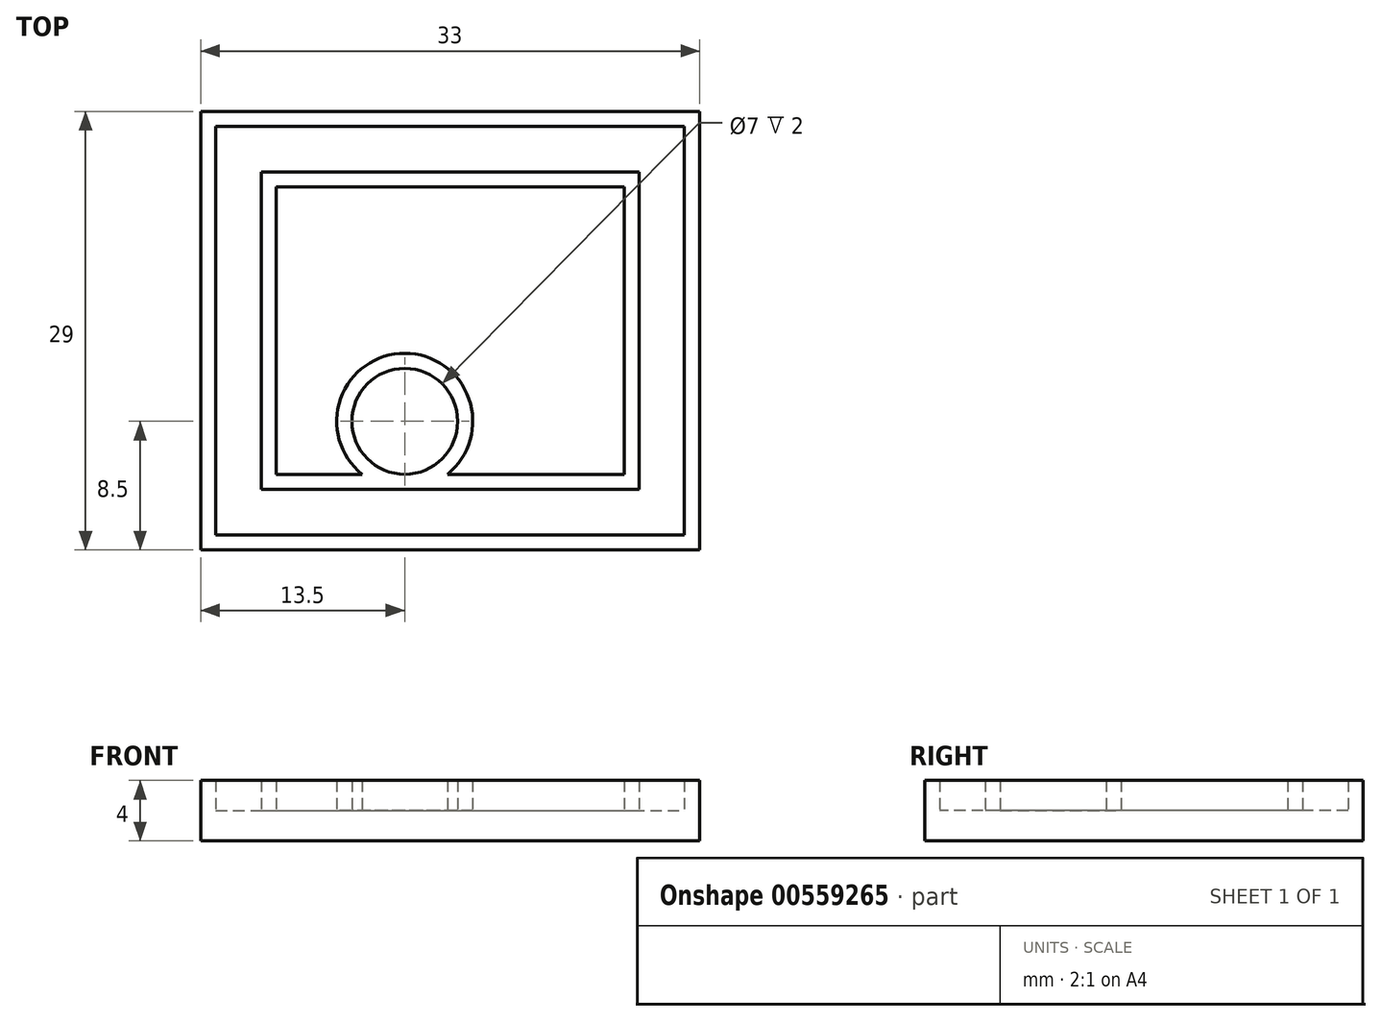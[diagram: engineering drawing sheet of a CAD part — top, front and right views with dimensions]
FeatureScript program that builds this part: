
annotation { "Feature Type Name" : "Feature", "Feature Type Description" : "" }
export const myFeature = defineFeature(function(context is Context, id is Id, definition is map)
    precondition{}
    {
        {
            var Q0;
            Q0=qCreatedBy(makeId("Top.planeOp"),FACE);
            var sketch = newSketch(context, id + "F0", { "sketchPlane" : qUnion([Q0])});
            skLineSegment(sketch, "E0.bottom", {"start": v(-16.5, 14.5) * mm, "end": v(16.5, 14.5) * mm});
            skLineSegment(sketch, "E0.top", {"start": v(-16.5, -14.5) * mm, "end": v(16.5, -14.5) * mm});
            skLineSegment(sketch, "E0.left", {"start": v(-16.5, 14.5) * mm, "end": v(-16.5, -14.5) * mm});
            skLineSegment(sketch, "E0.right", {"start": v(16.5, 14.5) * mm, "end": v(16.5, -14.5) * mm});
            skPoint(sketch, "E0.middle", {"position": v(0, 0) * mm});
            skSolve(sketch);
        }
        {
            var Q0;
            Q0 = qSketchRegion(id + "F0", true);
            extrude(context, id + "F1", {"entities" : qUnion([Q0]), "depth" : 2 * mm, "offsetDistance" : 25 * mm});
        }
        {
            var Q0;
            Q0=makeQuery(id+"F1.opExtrude","CAP_FACE",FACE,{"disambiguationData":[OSD([sQuery(id+"F0.wireOp",EDGE,"E0.bottom"),sQuery(id+"F0.wireOp",EDGE,"E0.top"),sQuery(id+"F0.wireOp",EDGE,"E0.left"),sQuery(id+"F0.wireOp",EDGE,"E0.right")])],"isStart":false});
            var sketch = newSketch(context, id + "F2", { "sketchPlane" : qUnion([Q0])});
            skLineSegment(sketch, "E1.bottom", {"start": v(-16.5, 14.5) * mm, "end": v(16.5, 14.5) * mm});
            skLineSegment(sketch, "E1.top", {"start": v(-16.5, -14.5) * mm, "end": v(16.5, -14.5) * mm});
            skLineSegment(sketch, "E1.left", {"start": v(-16.5, 14.5) * mm, "end": v(-16.5, -14.5) * mm});
            skLineSegment(sketch, "E1.right", {"start": v(16.5, 14.5) * mm, "end": v(16.5, -14.5) * mm});
            skLineSegment(sketch, "E2.bottom", {"start": v(-15.5, 13.5) * mm, "end": v(15.5, 13.5) * mm});
            skLineSegment(sketch, "E2.top", {"start": v(-15.5, -13.5) * mm, "end": v(15.5, -13.5) * mm});
            skLineSegment(sketch, "E2.left", {"start": v(-15.5, 13.5) * mm, "end": v(-15.5, -13.5) * mm});
            skLineSegment(sketch, "E2.right", {"start": v(15.5, 13.5) * mm, "end": v(15.5, -13.5) * mm});
            skLineSegment(sketch, "E3", {"start": v(-15.5, 13.5) * mm, "end": v(15.5, -13.5) * mm, "construction": true});
            skSolve(sketch);
        }
        {
            var Q0;
            Q0 = qSketchRegion(id + "F2", true);
            extrude(context, id + "F3", {"entities" : qUnion([Q0]), "operationType" : NewBodyOperationType.ADD, "depth" : 2 * mm, "offsetDistance" : 25 * mm});
        }
        {
            var Q0;
            Q0=makeQuery(id+"F1.opExtrude","CAP_FACE",FACE,{"disambiguationData":[OSD([sQuery(id+"F0.wireOp",EDGE,"E0.bottom"),sQuery(id+"F0.wireOp",EDGE,"E0.top"),sQuery(id+"F0.wireOp",EDGE,"E0.left"),sQuery(id+"F0.wireOp",EDGE,"E0.right")])],"isStart":false});
            var sketch = newSketch(context, id + "F4", { "sketchPlane" : qUnion([Q0])});
            skLineSegment(sketch, "E4.bottom", {"start": v(-11.5, 9.5) * mm, "end": v(11.5, 9.5) * mm});
            skLineSegment(sketch, "E4.top", {"start": v(-11.5, -9.5) * mm, "end": v(11.5, -9.5) * mm});
            skLineSegment(sketch, "E4.left", {"start": v(-11.5, 9.5) * mm, "end": v(-11.5, -9.5) * mm});
            skLineSegment(sketch, "E4.right", {"start": v(11.5, 9.5) * mm, "end": v(11.5, -9.5) * mm});
            skPoint(sketch, "E4.middle", {"position": v(0, 0) * mm});
            skLineSegment(sketch, "E5.bottom", {"start": v(-12.5, 10.5) * mm, "end": v(12.5, 10.5) * mm});
            skLineSegment(sketch, "E5.top", {"start": v(-12.5, -10.5) * mm, "end": v(12.5, -10.5) * mm});
            skLineSegment(sketch, "E5.left", {"start": v(-12.5, 10.5) * mm, "end": v(-12.5, -10.5) * mm});
            skLineSegment(sketch, "E5.right", {"start": v(12.5, 10.5) * mm, "end": v(12.5, -10.5) * mm});
            skSolve(sketch);
        }
        {
            var Q0;
            Q0 = qSketchRegion(id + "F4", true);
            extrude(context, id + "F5", {"entities" : qUnion([Q0]), "operationType" : NewBodyOperationType.ADD, "depth" : 2 * mm, "offsetDistance" : 25 * mm});
        }
        {
            var Q0;
            Q0=makeQuery(id+"F5.boolean.opBoolean","SPLIT",FACE,{"disambiguationData":[TD([makeQuery(id+"F5.opExtrude","SWEPT_FACE",FACE,{"disambiguationData":[OSD([sQuery(id+"F4.wireOp",EDGE,"E5.bottom")])]})])],"derivedFrom":makeQuery(id+"F1.opExtrude","CAP_FACE",FACE,{"disambiguationData":[OSD([sQuery(id+"F0.wireOp",EDGE,"E0.bottom"),sQuery(id+"F0.wireOp",EDGE,"E0.top"),sQuery(id+"F0.wireOp",EDGE,"E0.left"),sQuery(id+"F0.wireOp",EDGE,"E0.right")])],"isStart":false})});
            var sketch = newSketch(context, id + "F6", { "sketchPlane" : qUnion([Q0])});
            skCircle(sketch, "E6", {"center": v(-3, -6) * mm, "radius": 4.5 * mm});
            skCircle(sketch, "E7", {"center": v(-3, -6) * mm, "radius": 3.5 * mm});
            skSolve(sketch);
        }
        {
            var Q0;
            Q0 = qSketchRegion(id + "F6", true);
            extrude(context, id + "F7", {"entities" : qUnion([Q0]), "operationType" : NewBodyOperationType.ADD, "depth" : 2 * mm, "offsetDistance" : 25 * mm});
        }
    });
